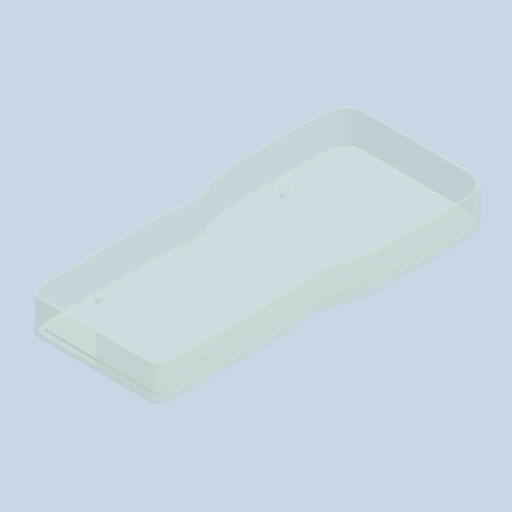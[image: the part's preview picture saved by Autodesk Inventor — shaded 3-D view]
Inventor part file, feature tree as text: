
AUTODESK INVENTOR PART (.ipt)
format: ipt  version: 2024 (Build 280153020, 153B)  size: 420,352 bytes
history: native  units: in
note: dims shown in document units (in); Inventor stores cm internally (conversion verified against a paired STEP export)
features: other x5, projected_geometry x4, sketch x2, shell x1, extrude x1
ambient origin geometry x8: Origin, YZ Plane, XZ Plane, XY Plane, X Axis, Y Axis, Z Axis, Center Point
bodies: Body1 (feature_tree)
feature tree (13):
  other  "Bottom"
  other  "Nokia3310.ipt"
  shell  "Shell1"  Thickness=0.3937in
  extrude  "Extrusion1"  Depth=0.0394in
  other  "Snap Fit1"
  other  "Bottom::Nokia3310.ipt"
  other  "TaggingFeature1"
  sketch  "Sketch2"  dims[d1=0.0394in d2=0.0394in d3=0.0344in]
  projected_geometry  "Projected Loop1"
  projected_geometry  "Projected Loop2"
  projected_geometry  "Projected Loop3"
  sketch  "Sketch3"  dims[d4=0.1969in d5=0.0787in d6=0.0394in d7=0.1181in d8=0.0591in d9=0.0197in d10=0.0197in d11=0.0197in]
  projected_geometry  "Projected Loop4"
